# Revit family: CONV_Pholc_GnrlPrpseLmnrs_Mobil70Pendant
name_source: partatom
category: Lighting Fixtures
revit_build: Autodesk Revit 2015 (Build: 20140606_1530(x64)
units: mm (PartAtom-declared; Revit-internal decimal feet)

## types (3) — shared parameters
Apparent Load = 0 VA
AssetType = Fixed
BIMObjectName = CONV_Pholc_GnrlPrpseLmnrs_Mobil70Pendant
Brand = Pholc
BulbIncluded = No
CableType = Textile cable
Category = Pendant
CeilingCup = Yes
CeilingPlug = Yes
Collection = Soft Reflections
ConvergoRefNr = 0103-1704-0002-SE
Designer = Monika Mulder
DurationUnit = Year
ExpiringDate = 07/2017
IfcExportAs = IfcLightFixtureType
IfcExportType = NOTDEFINED
LensMaterial = Glass, Frosted
LightFixtureMountingType = Suspended
LightFixturePlacingType = Ceiling
ManufacterURL = http://www.pholc.se
Manufacturer = Pholc
ManufacturerName = Pholc
NBSDescription = General purpose luminaires
NBSReference = 90-60-50/405
Name = GnrlPrpseLmnrs_Mobil70Pendant
NominalDepth = 457 mm  [stored 1.49934 ft]
NumberOfSources = 5
ProductInformation = Mobil is build up by four equal parts linked to each other. Together they create a pendant lamp with graphic
qualities and movement that looks interesting from all angles.
Shape = Sculptured
Size = 460x457x1000mm
Socket = G9 Base
TotalWattage = 20 W
URL = http://www.pholc.se
Uniclass2 = Pr_70_70_49_86
Uniclass2015Description = Pendant luminaires
Uniclass2015Reference = Pr_70_70_48_62
Version = 1
VersionDate = 05/04/2017
WarrantyDurationUnit = Year
Weight = 2,1 kg
zero-valued in all types: MaintenanceFactor

## per-type parameters (varying)
| type | ArticleNumber | Color | LightFixtureMainMaterial | LightFixtureSecondaryMaterial | Material | Model | ModelNumber | NominalHeight | NominalLength |
| Brass/opal glass | 510138 | Gold | Brass, Soft Yellow | Textile White | Brass | Mobil 70 Pendant | 510138 | 700 mm  [stored 2.29659 ft] | 460 mm  [stored 1.50919 ft] |
| Black/opal glass | 510135 | Black | Nickel Black | Textile Black | Nickel | Mobil 70 Pendant | 510135 | 1000 mm  [stored 3.28084 ft] | 700 mm  [stored 2.29659 ft] |
| Nickel/opal glass | 510134 | Grey | Nickel | Textile White | Nickel | Mobil 100 Pendant | 510134 | 1000 mm  [stored 3.28084 ft] | 700 mm  [stored 2.29659 ft] |

note: [stored X ft] marks values corroborated as IEEE doubles in the binary element streams (Revit-internal decimal feet)

## geometry (parser evidence)
native form markers: Sweep x6
no freeform markers — native parametric forms only
